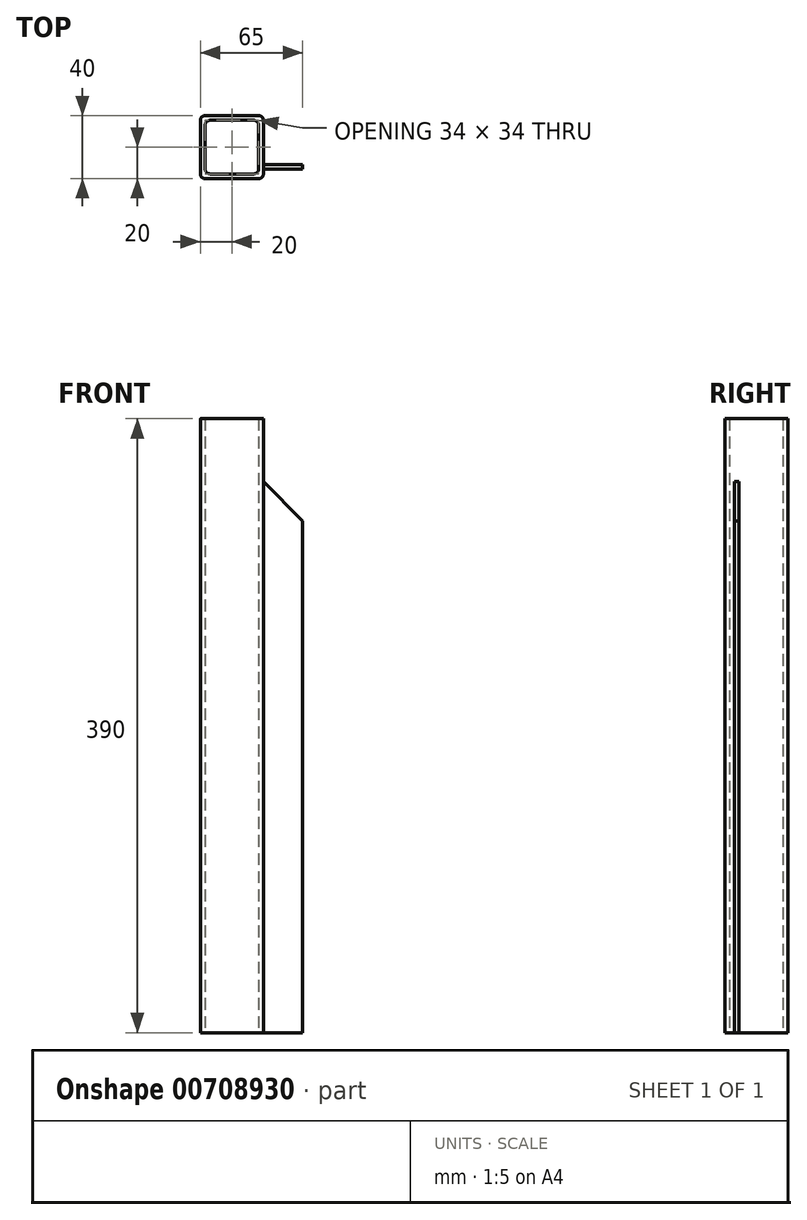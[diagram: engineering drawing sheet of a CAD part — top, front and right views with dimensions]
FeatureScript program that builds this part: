
annotation { "Feature Type Name" : "Feature", "Feature Type Description" : "" }
export const myFeature = defineFeature(function(context is Context, id is Id, definition is map)
    precondition{}
    {
        {
            var Q0;
            Q0=qCreatedBy(makeId("Top.planeOp"),FACE);
            var sketch = newSketch(context, id + "F0", { "sketchPlane" : qUnion([Q0])});
            skLineSegment(sketch, "E0.bottom", {"start": v(17, 20) * mm, "end": v(-17, 20) * mm});
            skLineSegment(sketch, "E0.top", {"start": v(17, -20) * mm, "end": v(-17, -20) * mm});
            skLineSegment(sketch, "E0.left", {"start": v(20, 17) * mm, "end": v(20, -17) * mm});
            skLineSegment(sketch, "E0.right", {"start": v(-20, 17) * mm, "end": v(-20, -17) * mm});
            skPoint(sketch, "E0.middle", {"position": v(0, 0) * mm});
            skLineSegment(sketch, "E1.0", {"start": v(17, 14) * mm, "end": v(17, -14) * mm});
            skLineSegment(sketch, "E1.1", {"start": v(14, 17) * mm, "end": v(-14, 17) * mm});
            skLineSegment(sketch, "E1.2", {"start": v(-17, 14) * mm, "end": v(-17, -14) * mm});
            skLineSegment(sketch, "E1.3", {"start": v(14, -17) * mm, "end": v(-14, -17) * mm});
            skPoint(sketch, "E2.visualSharp", {"position": v(17, 17) * mm});
            skArc(sketch, "E2.filletArc", {"start": v(17, 14) * mm, "mid": v(16.12, 16.12) * mm, "end": v(14, 17) * mm});
            skPoint(sketch, "E3.visualSharp", {"position": v(20, 20) * mm});
            skArc(sketch, "E3.filletArc", {"start": v(20, 17) * mm, "mid": v(19.12, 19.12) * mm, "end": v(17, 20) * mm});
            skPoint(sketch, "E4.visualSharp", {"position": v(17, -17) * mm});
            skArc(sketch, "E4.filletArc", {"start": v(14, -17) * mm, "mid": v(16.12, -16.12) * mm, "end": v(17, -14) * mm});
            skPoint(sketch, "E5.visualSharp", {"position": v(20, -20) * mm});
            skArc(sketch, "E5.filletArc", {"start": v(17, -20) * mm, "mid": v(19.12, -19.12) * mm, "end": v(20, -17) * mm});
            skPoint(sketch, "E6.visualSharp", {"position": v(-17, -17) * mm});
            skArc(sketch, "E6.filletArc", {"start": v(-17, -14) * mm, "mid": v(-16.12, -16.12) * mm, "end": v(-14, -17) * mm});
            skPoint(sketch, "E7.visualSharp", {"position": v(-20, -20) * mm});
            skArc(sketch, "E7.filletArc", {"start": v(-20, -17) * mm, "mid": v(-19.12, -19.12) * mm, "end": v(-17, -20) * mm});
            skPoint(sketch, "E8.visualSharp", {"position": v(-17, 17) * mm});
            skArc(sketch, "E8.filletArc", {"start": v(-14, 17) * mm, "mid": v(-16.12, 16.12) * mm, "end": v(-17, 14) * mm});
            skPoint(sketch, "E9.visualSharp", {"position": v(-20, 20) * mm});
            skArc(sketch, "E9.filletArc", {"start": v(-17, 20) * mm, "mid": v(-19.12, 19.12) * mm, "end": v(-20, 17) * mm});
            skSolve(sketch);
        }
        {
            var Q0;
            Q0 = qSketchRegion(id + "F0", true);
            extrude(context, id + "F1", {"entities" : qUnion([Q0]), "endBound" : BoundingType.SYMMETRIC, "depth" : 350 * mm, "offsetDistance" : 25 * mm});
        }
        {
            var Q0;
            Q0=makeQuery(id+"F1.opExtrude","SWEPT_FACE",FACE,{"disambiguationData":[OSD([sQuery(id+"F0.wireOp",EDGE,"E0.left")])]});
            var sketch = newSketch(context, id + "F2", { "sketchPlane" : qUnion([Q0])});
            skLineSegment(sketch, "E10", {"start": v(0, 175) * mm, "end": v(0, -175) * mm});
            skLineSegment(sketch, "E11.bottom", {"start": v(-14, 175) * mm, "end": v(-11, 175) * mm});
            skLineSegment(sketch, "E11.top", {"start": v(-14, -175) * mm, "end": v(-11, -175) * mm});
            skLineSegment(sketch, "E11.left", {"start": v(-14, 175) * mm, "end": v(-14, -175) * mm});
            skLineSegment(sketch, "E11.right", {"start": v(-11, 175) * mm, "end": v(-11, -175) * mm});
            skSolve(sketch);
        }
        {
            var Q0;
            Q0 = qSketchRegion(id + "F2", true);
            extrude(context, id + "F3", {"entities" : qUnion([Q0]), "operationType" : NewBodyOperationType.ADD, "depth" : 25 * mm, "offsetDistance" : 25 * mm});
        }
        {
            var Q0;
            Q0=makeQuery(id+"F3.opExtrude","SWEPT_FACE",FACE,{"disambiguationData":[OSD([sQuery(id+"F2.wireOp",EDGE,"E11.left")])]});
            var sketch = newSketch(context, id + "F4", { "sketchPlane" : qUnion([Q0])});
            skLineSegment(sketch, "E12", {"start": v(20, 175) * mm, "end": v(45, 150) * mm});
            skLineSegment(sketch, "E13", {"start": v(45, 150) * mm, "end": v(45, 175) * mm});
            skLineSegment(sketch, "E14", {"start": v(45, 175) * mm, "end": v(20, 175) * mm});
            skSolve(sketch);
        }
        {
            var Q0;
            Q0 = qSketchRegion(id + "F4", true);
            extrude(context, id + "F5", {"entities" : qUnion([Q0]), "operationType" : NewBodyOperationType.REMOVE, "endBound" : BoundingType.THROUGH_ALL, "oppositeDirection" : true, "depth" : 25 * mm, "offsetDistance" : 25 * mm});
        }
        {
            var Q0;
            {var subQ0=sQuery(id+"F2.wireOp",EDGE,"E11.bottom");Q0=makeQuery(id+"FJ2mqSL5vZxbPDw_1.1.F3.boolean.opBoolean","MERGE",FACE,{"derivedFrom":[makeQuery(id+"F3.boolean.opBoolean","MERGE",FACE,{"derivedFrom":[makeQuery(id+"F1.opExtrude","CAP_FACE",FACE,{"disambiguationData":[OSD([sQuery(id+"F0.wireOp",EDGE,"E0.bottom"),sQuery(id+"F0.wireOp",EDGE,"E0.top"),sQuery(id+"F0.wireOp",EDGE,"E0.left"),sQuery(id+"F0.wireOp",EDGE,"E0.right"),sQuery(id+"F0.wireOp",EDGE,"E1.0"),sQuery(id+"F0.wireOp",EDGE,"E1.1"),sQuery(id+"F0.wireOp",EDGE,"E1.2"),sQuery(id+"F0.wireOp",EDGE,"E1.3"),sQuery(id+"F0.wireOp",EDGE,"E2.filletArc"),sQuery(id+"F0.wireOp",EDGE,"E3.filletArc"),sQuery(id+"F0.wireOp",EDGE,"E4.filletArc"),sQuery(id+"F0.wireOp",EDGE,"E5.filletArc"),sQuery(id+"F0.wireOp",EDGE,"E6.filletArc"),sQuery(id+"F0.wireOp",EDGE,"E7.filletArc"),sQuery(id+"F0.wireOp",EDGE,"E8.filletArc"),sQuery(id+"F0.wireOp",EDGE,"E9.filletArc")])],"isStart":false}),makeQuery(id+"F3.opExtrude","SWEPT_FACE",FACE,{"disambiguationData":[OSD([subQ0])]})]}),makeQuery(id+"FJ2mqSL5vZxbPDw_1.1.F3.opExtrude","SWEPT_FACE",FACE,{"disambiguationData":[OSD([subQ0])]})]});}
            var sketch = newSketch(context, id + "F6", { "sketchPlane" : qUnion([Q0])});
            skArc(sketch, "E15.0", {"start": v(-20, -17) * mm, "mid": v(-19.12, -19.12) * mm, "end": v(-17, -20) * mm});
            skLineSegment(sketch, "E16.0", {"start": v(-20, 17) * mm, "end": v(-20, -17) * mm});
            skArc(sketch, "E17.0", {"start": v(-17, -14) * mm, "mid": v(-16.12, -16.12) * mm, "end": v(-14, -17) * mm});
            skLineSegment(sketch, "E18.0", {"start": v(-17, 14) * mm, "end": v(-17, -14) * mm});
            skLineSegment(sketch, "E19.0", {"start": v(14, -17) * mm, "end": v(-14, -17) * mm});
            skLineSegment(sketch, "E20.0", {"start": v(17, -20) * mm, "end": v(-17, -20) * mm});
            skArc(sketch, "E21.0", {"start": v(-14, 17) * mm, "mid": v(-16.12, 16.12) * mm, "end": v(-17, 14) * mm});
            skArc(sketch, "E22.0", {"start": v(-17, 20) * mm, "mid": v(-19.12, 19.12) * mm, "end": v(-20, 17) * mm});
            skLineSegment(sketch, "E23.0", {"start": v(17, 20) * mm, "end": v(-17, 20) * mm});
            skLineSegment(sketch, "E24.1", {"start": v(14, 17) * mm, "end": v(-14, 17) * mm});
            skArc(sketch, "E25.0", {"start": v(17, 14) * mm, "mid": v(16.12, 16.12) * mm, "end": v(14, 17) * mm});
            skArc(sketch, "E26.0", {"start": v(20, 17) * mm, "mid": v(19.12, 19.12) * mm, "end": v(17, 20) * mm});
            skLineSegment(sketch, "E27.0", {"start": v(17, 14) * mm, "end": v(17, -14) * mm});
            skLineSegment(sketch, "E28.0", {"start": v(20, 17) * mm, "end": v(20, -11) * mm});
            skArc(sketch, "E29.0", {"start": v(14, -17) * mm, "mid": v(16.12, -16.12) * mm, "end": v(17, -14) * mm});
            skArc(sketch, "E30.0", {"start": v(17, -20) * mm, "mid": v(19.12, -19.12) * mm, "end": v(20, -17) * mm});
            skLineSegment(sketch, "E31.0", {"start": v(20, -11) * mm, "end": v(20, -14) * mm});
            skLineSegment(sketch, "E32.0", {"start": v(20, -14) * mm, "end": v(20, -17) * mm});
            skSolve(sketch);
        }
        {
            var Q0;
            Q0 = qSketchRegion(id + "F6", true);
            extrude(context, id + "F7", {"entities" : qUnion([Q0]), "operationType" : NewBodyOperationType.ADD, "depth" : 40 * mm, "offsetDistance" : 25 * mm});
        }
    });
